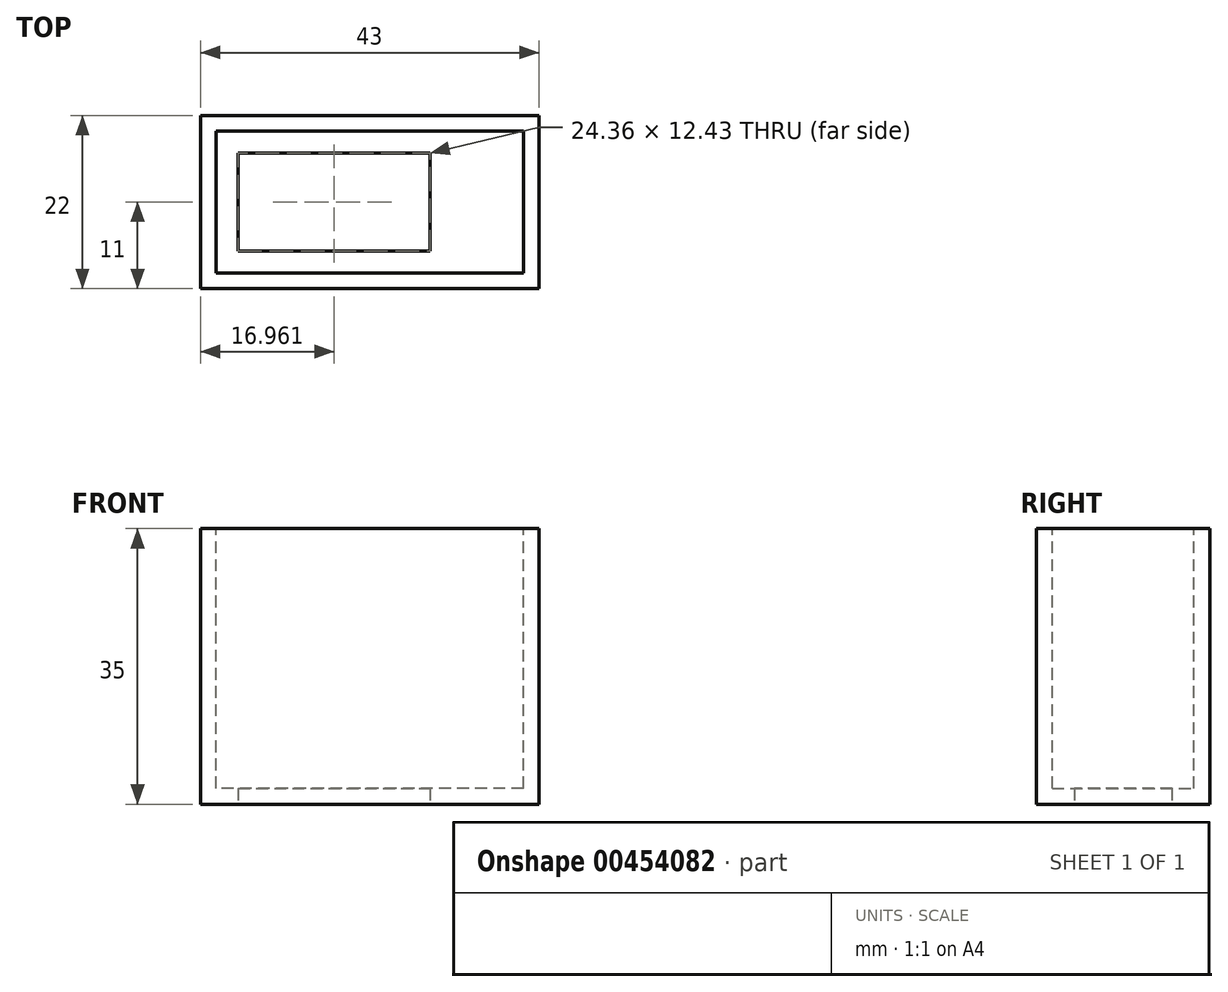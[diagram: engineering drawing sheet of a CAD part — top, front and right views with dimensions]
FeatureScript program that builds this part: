
annotation { "Feature Type Name" : "Feature", "Feature Type Description" : "" }
export const myFeature = defineFeature(function(context is Context, id is Id, definition is map)
    precondition{}
    {
        {
            var Q0;
            Q0=qCreatedBy(makeId("Top.planeOp"),FACE);
            var sketch = newSketch(context, id + "F0", { "sketchPlane" : qUnion([Q0])});
            skLineSegment(sketch, "E0.bottom", {"start": v(21.5, -11) * mm, "end": v(-21.5, -11) * mm});
            skLineSegment(sketch, "E0.top", {"start": v(21.5, 11) * mm, "end": v(-21.5, 11) * mm});
            skLineSegment(sketch, "E0.left", {"start": v(21.5, -11) * mm, "end": v(21.5, 11) * mm});
            skLineSegment(sketch, "E0.right", {"start": v(-21.5, -11) * mm, "end": v(-21.5, 11) * mm});
            skPoint(sketch, "E0.middle", {"position": v(0, 0) * mm});
            skSolve(sketch);
        }
        {
            var Q0;
            Q0 = qSketchRegion(id + "F0", true);
            extrude(context, id + "F1", {"entities" : qUnion([Q0]), "depth" : 35 * mm});
        }
        {
            var Q0;
            Q0=makeQuery(id+"F1.opExtrude","CAP_FACE",FACE,{"disambiguationData":[OSD([sQuery(id+"F0.wireOp",EDGE,"E0.bottom"),sQuery(id+"F0.wireOp",EDGE,"E0.top"),sQuery(id+"F0.wireOp",EDGE,"E0.left"),sQuery(id+"F0.wireOp",EDGE,"E0.right")])],"isStart":false});
            var sketch = newSketch(context, id + "F2", { "sketchPlane" : qUnion([Q0])});
            skLineSegment(sketch, "E1.bottom", {"start": v(19.5, -9) * mm, "end": v(-19.5, -9) * mm});
            skLineSegment(sketch, "E1.top", {"start": v(19.5, 9) * mm, "end": v(-19.5, 9) * mm});
            skLineSegment(sketch, "E1.left", {"start": v(19.5, -9) * mm, "end": v(19.5, 9) * mm});
            skLineSegment(sketch, "E1.right", {"start": v(-19.5, -9) * mm, "end": v(-19.5, 9) * mm});
            skPoint(sketch, "E1.middle", {"position": v(0, 0) * mm});
            skSolve(sketch);
        }
        {
            var Q0;
            Q0=makeQuery(id+"F2.imprint","IMPRINT",FACE,{"disambiguationData":[TD([[makeQuery(id+"F2.imprint","IMPRINT",EDGE,{"derivedFrom":sQuery(id+"F2.wireOp",EDGE,"E1.bottom")}),-1.0]])]});
            extrude(context, id + "F3", {"entities" : qUnion([Q0]), "operationType" : NewBodyOperationType.REMOVE, "oppositeDirection" : true, "depth" : 33 * mm});
        }
        {
            var Q0;
            Q0=qCreatedBy(makeId("Top.planeOp"),FACE);
            var sketch = newSketch(context, id + "F4", { "sketchPlane" : qUnion([Q0])});
            skLineSegment(sketch, "E2.bottom", {"start": v(7.64, -6.21) * mm, "end": v(-16.72, -6.21) * mm});
            skLineSegment(sketch, "E2.top", {"start": v(7.64, 6.21) * mm, "end": v(-16.72, 6.21) * mm});
            skLineSegment(sketch, "E2.left", {"start": v(7.64, -6.21) * mm, "end": v(7.64, 6.21) * mm});
            skLineSegment(sketch, "E2.right", {"start": v(-16.72, -6.21) * mm, "end": v(-16.72, 6.21) * mm});
            skPoint(sketch, "E2.middle", {"position": v(-4.54, 0) * mm});
            skSolve(sketch);
        }
        {
            var Q0;
            Q0 = qSketchRegion(id + "F4", true);
            extrude(context, id + "F5", {"entities" : qUnion([Q0]), "operationType" : NewBodyOperationType.REMOVE, "depth" : 25 * mm});
        }
    });
